# Revit family: Universal-Showering_U495D-BL60-PK
name_source: partatom
category: Generic Models
revit_build: Autodesk Revit MEP 2013 (Build: 20130531_2115(x64)
units: mm (PartAtom-declared; Revit-internal decimal feet)

## types (7) — shared parameters
Base = Matte Black
Default Elevation = 1524 mm  [stored 5 ft]
Description = Universal Showering
Manufacturer = Delta
URL = www.deltafaucet.com

## per-type parameters (varying)
| type | Model | Unit |
| Chrome | U495D-BL60-PK | Metal - Chrome |
| Matte Black | U495D-BL60-PK | Matte Black |
| Champagne Bronze | U495D-CZ60-PK | Bronze |
| Polished Brass | U495D-PB60-PK | Brass, Soft Yellow, Welded |
| Polished Nickel | U495D-PN60-PK | Nickel-Brizo-Metal-Brushed |
| Venetian Bronze | U495D-RB60-PK | Bronze-Brizo-Metal-Brilliance-Brushed |
| Stainless | U495D-SS60-PK | Stainless Steel |

note: [stored X ft] marks values corroborated as IEEE doubles in the binary element streams (Revit-internal decimal feet)

## geometry (parser evidence)
native form markers: Blend x47, Sweep x4
no freeform markers — native parametric forms only
